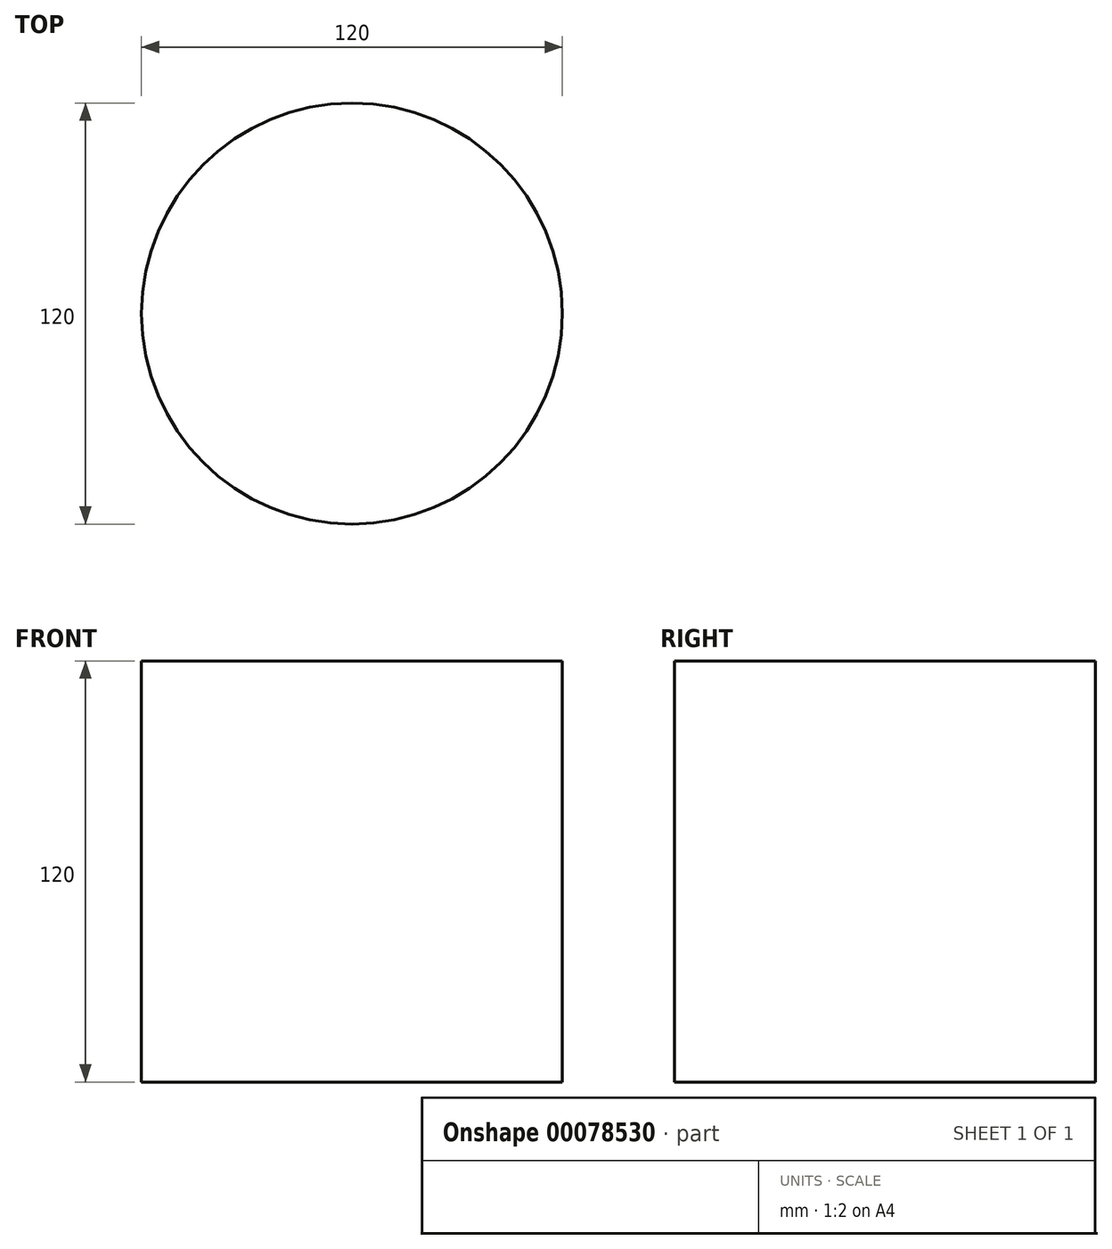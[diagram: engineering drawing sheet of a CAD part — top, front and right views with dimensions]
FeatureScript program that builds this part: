
annotation { "Feature Type Name" : "Feature", "Feature Type Description" : "" }
export const myFeature = defineFeature(function(context is Context, id is Id, definition is map)
    precondition{}
    {
        {
            var Q0;
            Q0=qCreatedBy(makeId("Right.planeOp"),FACE);
            var sketch = newSketch(context, id + "F0", { "sketchPlane" : qUnion([Q0])});
            skLineSegment(sketch, "E0.bottom", {"start": v(0, 0) * mm, "end": v(60, 0) * mm});
            skLineSegment(sketch, "E0.top", {"start": v(0, 120) * mm, "end": v(60, 120) * mm});
            skLineSegment(sketch, "E0.left", {"start": v(0, 0) * mm, "end": v(0, 120) * mm});
            skLineSegment(sketch, "E0.right", {"start": v(60, 0) * mm, "end": v(60, 120) * mm});
            skLineSegment(sketch, "E1", {"start": v(0, -29.63) * mm, "end": v(0, 141.29) * mm});
            skSolve(sketch);
        }
        {
            var Q0;
            {var subQ0=sQuery(id+"F0.wireOp",EDGE,"E0.bottom");Q0=makeQuery(id+"F0.imprint","IMPRINT",FACE,{"disambiguationData":[TD([[makeQuery(id+"F0.imprint","IMPRINT",EDGE,{"derivedFrom":subQ0}),1.0]])]});}
            var Q1;
            Q1=sQuery(id+"F0.wireOp",EDGE,"E1");
            revolve(context, id + "F1", {"entities" : qUnion([Q0]), "axis" : qUnion([Q1]), "revolveType" : RevolveType.ONE_DIRECTION, "angle" : 360 * degree});
        }
    });
